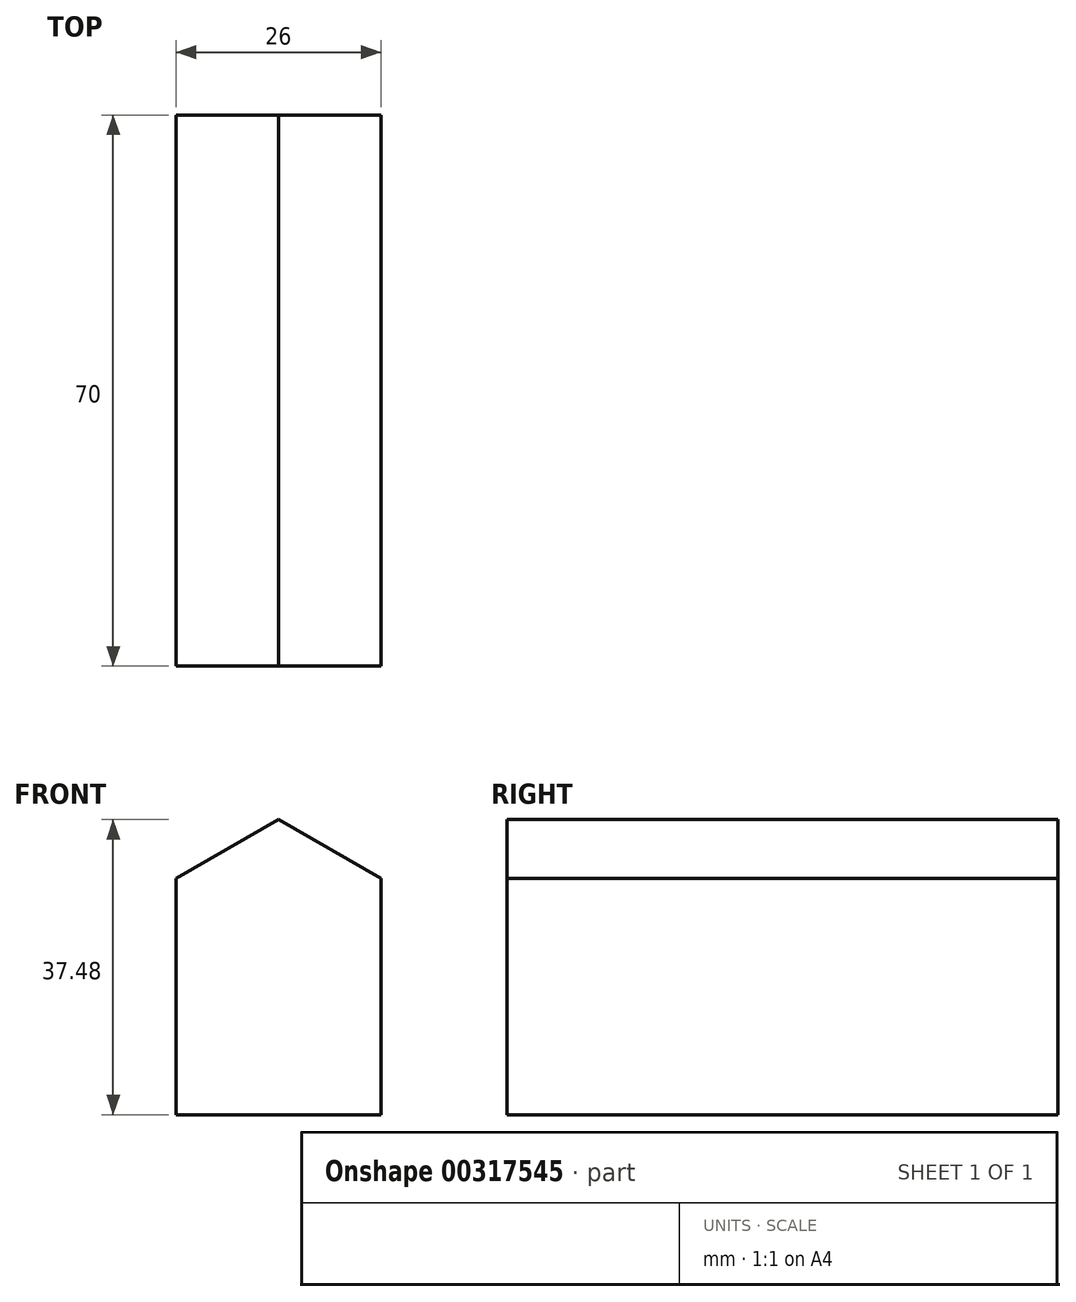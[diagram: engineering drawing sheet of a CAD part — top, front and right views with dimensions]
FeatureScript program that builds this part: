
annotation { "Feature Type Name" : "Feature", "Feature Type Description" : "" }
export const myFeature = defineFeature(function(context is Context, id is Id, definition is map)
    precondition{}
    {
        {
            var Q0;
            Q0=qCreatedBy(makeId("Front.planeOp"),FACE);
            var sketch = newSketch(context, id + "F0", { "sketchPlane" : qUnion([Q0])});
            skLineSegment(sketch, "E0", {"start": v(0, 0) * mm, "end": v(0, 30) * mm});
            skLineSegment(sketch, "E1", {"start": v(0, 30) * mm, "end": v(13, 37.48) * mm});
            skLineSegment(sketch, "E2", {"start": v(13, 37.48) * mm, "end": v(26, 30) * mm});
            skLineSegment(sketch, "E3", {"start": v(26, 30) * mm, "end": v(26, 0) * mm});
            skLineSegment(sketch, "E4", {"start": v(26, 0) * mm, "end": v(0, 0) * mm});
            skSolve(sketch);
        }
        {
            var Q0;
            Q0=makeQuery(id+"F0.imprint","IMPRINT",FACE,{"disambiguationData":[TD([[makeQuery(id+"F0.imprint","IMPRINT",EDGE,{"derivedFrom":sQuery(id+"F0.wireOp",EDGE,"E0")}),-1.0]])]});
            extrude(context, id + "F1", {"entities" : qUnion([Q0]), "depth" : 70 * mm});
        }
    });
